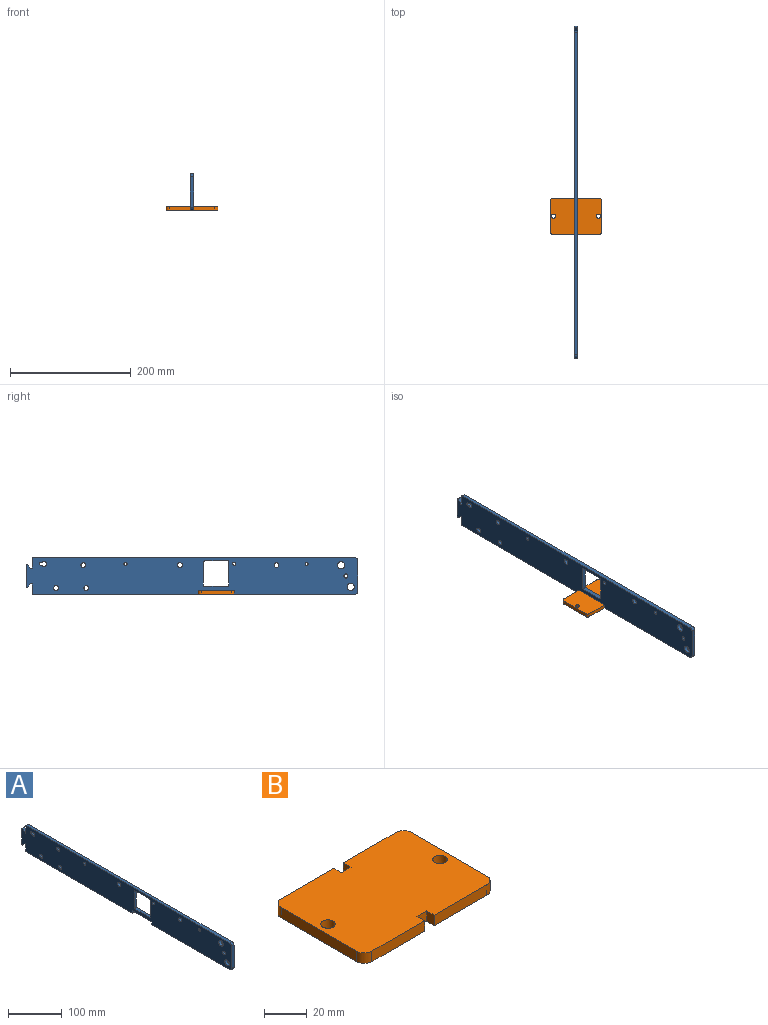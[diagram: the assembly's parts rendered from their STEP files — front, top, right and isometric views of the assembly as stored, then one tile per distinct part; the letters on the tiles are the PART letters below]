
ASSEMBLY  parts=2 mates=1
PART A: 43 faces, bbox 6x550x60 mm
  f0: plane 38x6mm, normal (0,-1,0), area 228mm2, adj f29,f30,f36,f42
  f1: plane 38x6mm, normal (0,0,-1), area 228mm2, adj f29,f30,f41,f42
  f2: plane 38x6mm, normal (0,1,0), area 228mm2, adj f29,f30,f39,f41
  f3: plane 50.4x6mm, normal (0,0,-1), area 302.4mm2, adj f4,f27,f29,f30
  f4: plane 6x6mm, normal (0,1,0), area 36mm2, adj f3,f5,f29,f30
  f5: plane 204.8x6mm, normal (0,0,-1), area 1228.8mm2, adj f4,f29,f30,f37
  f6: plane 50x6mm, normal (0,-1,0), area 300mm2, adj f29,f30,f37,f38
  f7: plane 533.95x6mm, normal (0,0,1), area 3203.7mm2, adj f29,f30,f32,f38
  f8: plane 15.79x6mm, normal (0,1,0), area 94.7mm2, adj f29,f30,f32,f33
  f9: plane 6.42x6.42mm, normal (0,-0.71,0.71), area 54.4mm2, adj f29,f30,f33,f34
  f10: plane 36.29x6mm, normal (0,1,0), area 217.7mm2, adj f29,f30,f34,f35
  f11: plane 6.42x6.42mm, normal (0,-0.71,-0.71), area 54.4mm2, adj f29,f30,f35,f40
  f12: plane 15.79x6mm, normal (0,1,0), area 94.7mm2, adj f29,f30,f31,f40
  f13: plane 278.75x6mm, normal (0,0,-1), area 1672.5mm2, adj f27,f29,f30,f31
  f14: cylinder r=4.05mm len=8.1mm, axis (1,0,0), area 125.6mm2, adj f23,f29,f30
  f15: cylinder r=2.65mm len=6mm, axis (1,0,0), area 99.9mm2, adj f29,f30
  f16: cylinder r=2.65mm len=6mm, axis (1,0,0), area 99.9mm2, adj f29,f30
  f17: cylinder r=2.65mm len=6mm, axis (1,0,0), area 99.9mm2, adj f29,f30
  f18: cylinder r=6.03mm len=12.05mm, axis (1,0,0), area 227.1mm2, adj f29,f30
  f19: cylinder r=6.03mm len=12.05mm, axis (1,0,0), area 227.1mm2, adj f29,f30
  f20: cylinder r=3.4mm len=6.8mm, axis (1,0,0), area 128.2mm2, adj f29,f30
  f21: cylinder r=4.05mm len=8.1mm, axis (1,0,0), area 152.7mm2, adj f29,f30
  f22: cylinder r=4.05mm len=8.1mm, axis (1,0,0), area 152.7mm2, adj f29,f30
  f23: cylinder r=2.65mm len=6mm, axis (1,0,0), area 70mm2, adj f14,f29,f30
  f24: cylinder r=4.05mm len=8.1mm, axis (1,0,0), area 152.7mm2, adj f29,f30
  f25: cylinder r=4.05mm len=8.1mm, axis (1,0,0), area 152.7mm2, adj f29,f30
  f26: cylinder r=4.05mm len=8.1mm, axis (1,0,0), area 152.7mm2, adj f29,f30
  f27: plane 6x6mm, normal (0,-1,0), area 36mm2, adj f3,f13,f29,f30
  f28: plane 38x6mm, normal (0,0,1), area 228mm2, adj f29,f30,f36,f39
  f29: plane 549.95x60mm, normal (-1,0,0), area 29977.8mm2, adj f0,f1,f2,f3,f4,f5,f6,f7
  f30: plane 549.95x60mm, normal (1,0,0), area 29977.8mm2, adj f0,f1,f2,f3,f4,f5,f6,f7
  f31: cylinder r=1mm len=6mm, axis (-1,0,0), area 9.4mm2, adj f12,f13,f29,f30
  f32: cylinder r=1mm len=6mm, axis (1,0,0), area 9.4mm2, adj f7,f8,f29,f30
  f33: cylinder r=1.1mm len=6mm, axis (1,0,0), area 15.6mm2, adj f8,f9,f29,f30
  f34: cylinder r=1mm len=6mm, axis (-1,0,0), area 14.1mm2, adj f9,f10,f29,f30
  f35: cylinder r=1mm len=6mm, axis (1,0,0), area 14.1mm2, adj f10,f11,f29,f30
  f36: cylinder r=2mm len=6mm, axis (-1,0,0), area 18.8mm2, adj f0,f28,f29,f30
  f37: cylinder r=5mm len=6mm, axis (-1,0,0), area 47.1mm2, adj f5,f6,f29,f30
  f38: cylinder r=5mm len=6mm, axis (1,0,0), area 47.1mm2, adj f6,f7,f29,f30
  f39: cylinder r=2mm len=6mm, axis (1,0,0), area 18.8mm2, adj f2,f28,f29,f30
  f40: cylinder r=1.1mm len=6mm, axis (-1,0,0), area 15.6mm2, adj f11,f12,f29,f30
  f41: cylinder r=2mm len=6mm, axis (-1,0,0), area 18.8mm2, adj f1,f2,f29,f30
  f42: cylinder r=2mm len=6mm, axis (1,0,0), area 18.8mm2, adj f0,f1,f29,f30
PART B: 20 faces, bbox 86x60x6 mm
  f0: plane 6x5mm, normal (-1,0,0), area 30mm2, adj f1,f13,f14,f15
  f1: plane 6.4x6mm, normal (0,-1,0), area 38.4mm2, adj f0,f2,f14,f15
  f2: plane 6x5mm, normal (1,0,0), area 30mm2, adj f1,f3,f14,f15
  f3: plane 34.8x6mm, normal (0,-1,0), area 208.8mm2, adj f2,f14,f15,f17
  f4: plane 50x6mm, normal (-1,0,0), area 300mm2, adj f14,f15,f16,f17
  f5: plane 34.8x6mm, normal (0,1,0), area 208.8mm2, adj f6,f14,f15,f16
  f6: plane 6x5mm, normal (1,0,0), area 30mm2, adj f5,f7,f14,f15
  f7: plane 6.4x6mm, normal (0,1,0), area 38.4mm2, adj f6,f8,f14,f15
  f8: plane 6x5mm, normal (-1,0,0), area 30mm2, adj f7,f9,f14,f15
  f9: plane 34.8x6mm, normal (0,1,0), area 208.8mm2, adj f8,f14,f15,f18
  f10: plane 50x6mm, normal (1,0,0), area 300mm2, adj f14,f15,f18,f19
  f11: cylinder r=3.4mm len=6.8mm, axis (0,0,-1), area 128.2mm2, adj f14,f15
  f12: cylinder r=3.4mm len=6.8mm, axis (0,0,-1), area 128.2mm2, adj f14,f15
  f13: plane 34.8x6mm, normal (0,-1,0), area 208.8mm2, adj f0,f14,f15,f19
  f14: plane 86x60mm, normal (0,0,-1), area 5001.9mm2, adj f0,f1,f2,f3,f4,f5,f6,f7
  f15: plane 86x60mm, normal (0,0,1), area 5001.9mm2, adj f0,f1,f2,f3,f4,f5,f6,f7
  f16: cylinder r=5mm len=6mm, axis (0,0,1), area 47.1mm2, adj f4,f5,f14,f15
  f17: cylinder r=5mm len=6mm, axis (0,0,-1), area 47.1mm2, adj f3,f4,f14,f15
  f18: cylinder r=5mm len=6mm, axis (0,0,-1), area 47.1mm2, adj f9,f10,f14,f15
  f19: cylinder r=5mm len=6mm, axis (0,0,1), area 47.1mm2, adj f10,f13,f14,f15
PLACE A at identity
PLACE B t=(0,-600,0)mm
MATE fastened B.f15 <-> A.f3  axis (0,0,1) through (3,-300,-29)mm
